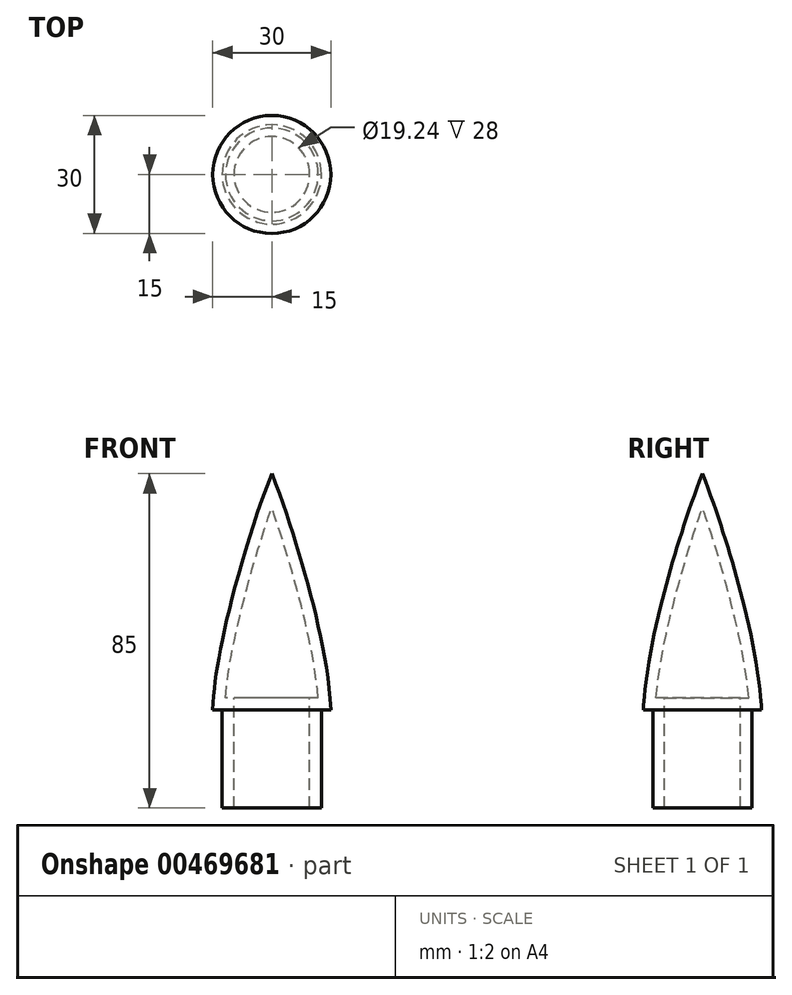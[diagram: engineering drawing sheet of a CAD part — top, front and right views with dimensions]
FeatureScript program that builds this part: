
annotation { "Feature Type Name" : "Feature", "Feature Type Description" : "" }
export const myFeature = defineFeature(function(context is Context, id is Id, definition is map)
    precondition{}
    {
        {
            var Q0;
            Q0=qCreatedBy(makeId("Front.planeOp"),FACE);
            var sketch = newSketch(context, id + "F0", { "sketchPlane" : qUnion([Q0])});
            skLineSegment(sketch, "E0", {"start": v(0, 0) * mm, "end": v(0, 42.5) * mm, "construction": true});
            skLineSegment(sketch, "E1", {"start": v(0, 0) * mm, "end": v(6.17, 0) * mm, "construction": true});
            skLineSegment(sketch, "E2.MirrorCS", {"start": v(0, 0) * mm, "end": v(0, -42.5) * mm, "construction": true});
            skLineSegment(sketch, "E3", {"start": v(0, -42.5) * mm, "end": v(12.62, -42.5) * mm});
            skLineSegment(sketch, "E4.MirrorCS", {"start": v(0, -42.5) * mm, "end": v(-12.62, -42.5) * mm});
            skPoint(sketch, "E5", {"position": v(0, -17.5) * mm});
            skLineSegment(sketch, "E6", {"start": v(12.62, -17.5) * mm, "end": v(15, -17.5) * mm});
            skLineSegment(sketch, "E7.MirrorCS", {"start": v(-12.62, -17.5) * mm, "end": v(-15, -17.5) * mm});
            skLineSegment(sketch, "E8", {"start": v(-12.62, -42.5) * mm, "end": v(-12.62, -17.5) * mm});
            skLineSegment(sketch, "E9.MirrorCS", {"start": v(12.62, -42.5) * mm, "end": v(12.62, -17.5) * mm});
            skFitSpline(sketch, "E10", {"points": [v(-15, -17.5) * mm, v(-12.62, 0) * mm, v(0, 42.5) * mm], "startDerivative": vector(2.08, 40.67) * mm, "endDerivative": vector(28.98, 74.82) * mm});
            skFitSpline(sketch, "E11.MirrorCS", {"points": [v(15, -17.5) * mm, v(12.62, 0) * mm, v(0, 42.5) * mm], "startDerivative": vector(-2.08, 40.67) * mm, "endDerivative": vector(-28.98, 74.82) * mm});
            skLineSegment(sketch, "E12", {"start": v(0, 42.5) * mm, "end": v(0, -42.5) * mm});
            skSolve(sketch);
        }
        {
            var Q0;
            Q0=makeQuery(id+"F0.imprint","IMPRINT",FACE,{"disambiguationData":[TD([[makeQuery(id+"F0.imprint","IMPRINT",EDGE,{"derivedFrom":sQuery(id+"F0.wireOp",EDGE,"E4.MirrorCS")}),-1.0]])]});
            var Q1;
            Q1=sQuery(id+"F0.wireOp",EDGE,"E12");
            revolve(context, id + "F1", {"entities" : qUnion([Q0]), "axis" : qUnion([Q1]), "revolveType" : RevolveType.FULL});
        }
        {
            var Q0;
            Q0=makeQuery(id+"F1.opRevolve","SWEPT_FACE",FACE,{"disambiguationData":[OSD([sQuery(id+"F0.wireOp",EDGE,"E4.MirrorCS")])]});
            shell(context, id + "F2", {"entities" : qUnion([Q0]), "thickness" : 3 * mm});
        }
    });
